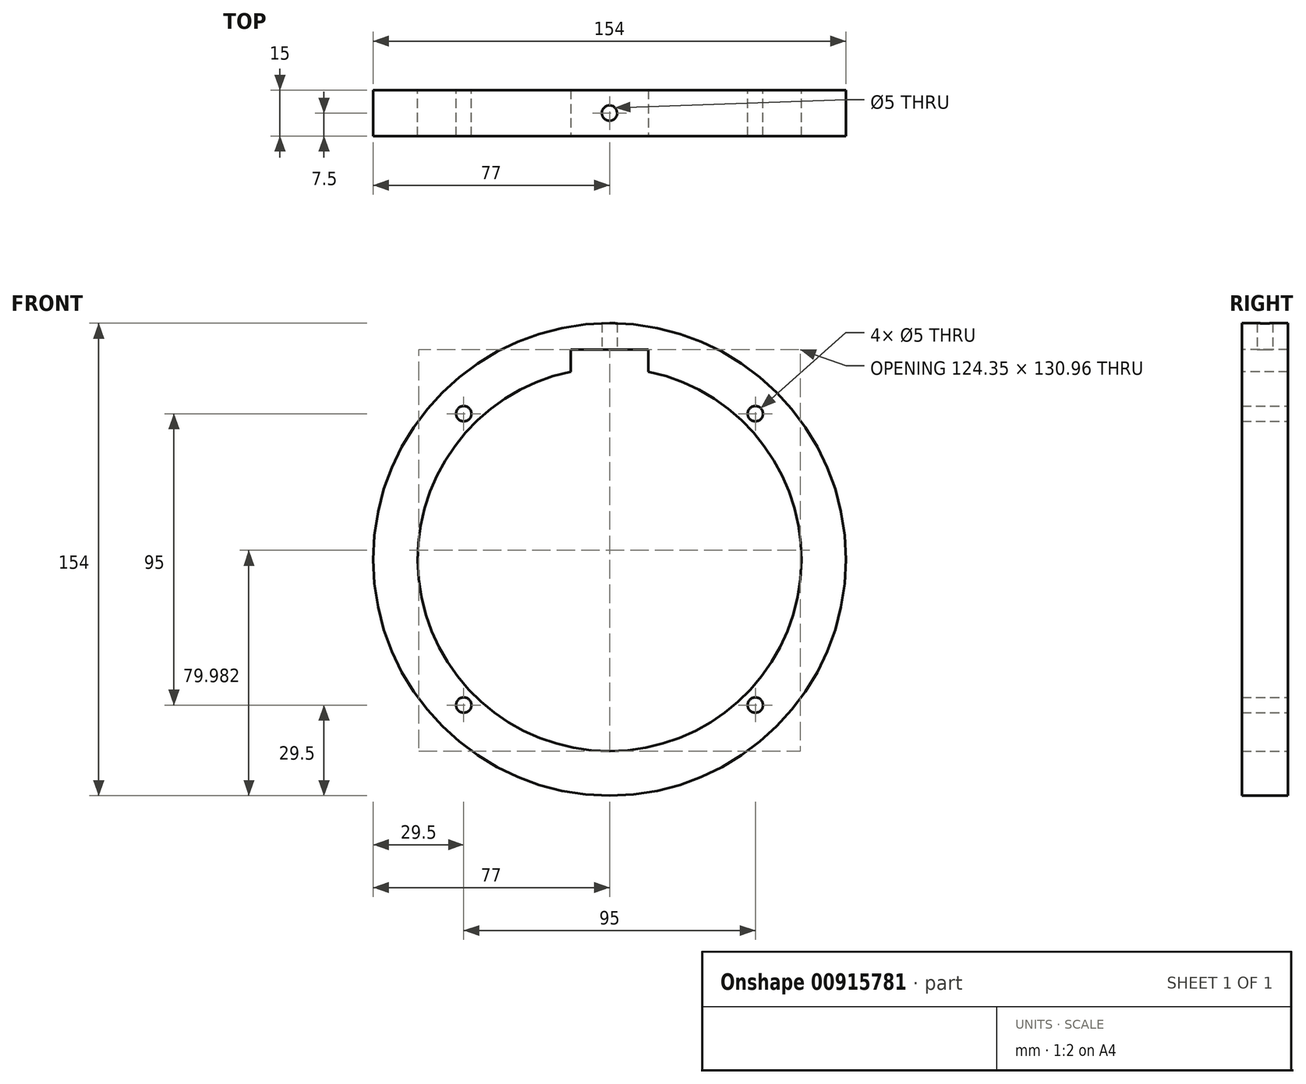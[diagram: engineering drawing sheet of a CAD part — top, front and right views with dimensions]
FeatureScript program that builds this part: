
annotation { "Feature Type Name" : "Feature", "Feature Type Description" : "" }
export const myFeature = defineFeature(function(context is Context, id is Id, definition is map)
    precondition{}
    {
        {
            var Q0;
            Q0=qCreatedBy(makeId("Front.planeOp"),FACE);
            var sketch = newSketch(context, id + "F0", { "sketchPlane" : qUnion([Q0])});
            skCircle(sketch, "E0", {"center": v(0, 0) * mm, "radius": 77 * mm});
            skCircle(sketch, "E1", {"center": v(0, 0) * mm, "radius": 62.5 * mm});
            skSolve(sketch);
        }
        {
            var Q0;
            Q0=makeQuery(id+"F0.imprint","IMPRINT",FACE,{"disambiguationData":[TD([[makeQuery(id+"F0.imprint","IMPRINT",EDGE,{"derivedFrom":sQuery(id+"F0.wireOp",EDGE,"E0")}),1.0]])]});
            extrude(context, id + "F1", {"entities" : qUnion([Q0]), "depth" : 15 * mm, "offsetDistance" : 25 * mm});
        }
        {
            var Q0;
            Q0=qCreatedBy(makeId("Front.planeOp"),FACE);
            var sketch = newSketch(context, id + "F2", { "sketchPlane" : qUnion([Q0])});
            skLineSegment(sketch, "E2.bottom", {"start": v(-47.5, 47.5) * mm, "end": v(47.5, 47.5) * mm, "construction": true});
            skLineSegment(sketch, "E2.top", {"start": v(-47.5, -47.5) * mm, "end": v(47.5, -47.5) * mm, "construction": true});
            skLineSegment(sketch, "E2.left", {"start": v(-47.5, 47.5) * mm, "end": v(-47.5, -47.5) * mm, "construction": true});
            skLineSegment(sketch, "E2.right", {"start": v(47.5, 47.5) * mm, "end": v(47.5, -47.5) * mm, "construction": true});
            skPoint(sketch, "E2.middle", {"position": v(0, 0) * mm});
            skSolve(sketch);
        }
        {
            var Q0;
            Q0=sQuery(id+"F2.wireOp",VERTEX,"E2.bottom.start");
            var Q1;
            Q1=sQuery(id+"F2.wireOp",VERTEX,"E2.bottom.end");
            var Q2;
            Q2=sQuery(id+"F2.wireOp",VERTEX,"E2.top.end");
            var Q3;
            Q3=sQuery(id+"F2.wireOp",VERTEX,"E2.top.start");
            var Q4;
            Q4=makeQuery(id+"F1.opExtrude","SWEPT_BODY",BODY,{"disambiguationData":[OSD([sQuery(id+"F0.wireOp",EDGE,"E0"),sQuery(id+"F0.wireOp",EDGE,"E1")])]});
            hole(context, id + "F3", {"style" : HoleStyle.SIMPLE, "endStyle" : HoleEndStyle.THROUGH, "oppositeDirection" : true, "holeDiameter" : 5 * mm, "majorDiameter" : 5 * mm, "isTappedThrough" : true, "tappedDepth" : 12 * mm, "tapClearance" : 3, "locations" : qUnion([Q0, Q1, Q2, Q3]), "scope" : qUnion([Q4])});
        }
        {
            var Q0;
            Q0=makeQuery(id+"F1.opExtrude","CAP_FACE",FACE,{"disambiguationData":[OSD([sQuery(id+"F0.wireOp",EDGE,"E0"),sQuery(id+"F0.wireOp",EDGE,"E1")])],"isStart":false});
            var sketch = newSketch(context, id + "F4", { "sketchPlane" : qUnion([Q0])});
            skLineSegment(sketch, "E3.bottom", {"start": v(-12.66, 68.46) * mm, "end": v(12.66, 68.46) * mm});
            skLineSegment(sketch, "E3.top", {"start": v(-12.66, 45.6) * mm, "end": v(12.66, 45.6) * mm});
            skLineSegment(sketch, "E3.left", {"start": v(-12.66, 68.46) * mm, "end": v(-12.66, 45.6) * mm});
            skLineSegment(sketch, "E3.right", {"start": v(12.66, 68.46) * mm, "end": v(12.66, 45.6) * mm});
            skPoint(sketch, "E3.middle", {"position": v(0, 57.03) * mm});
            skSolve(sketch);
        }
        {
            var Q0;
            {var subQ0=sQuery(id+"F4.wireOp",EDGE,"E3.bottom");Q0=makeQuery(id+"F4.imprint","IMPRINT",FACE,{"disambiguationData":[TD([[makeQuery(id+"F4.imprint","IMPRINT",EDGE,{"derivedFrom":subQ0}),-1.0]])]});}
            extrude(context, id + "F5", {"entities" : qUnion([Q0]), "operationType" : NewBodyOperationType.REMOVE, "oppositeDirection" : true, "depth" : 25 * mm, "offsetDistance" : 25 * mm});
        }
        {
            var Q0;
            Q0=makeQuery(id+"F5.boolean.opBoolean","COPY",FACE,{"derivedFrom":makeQuery(id+"F5.opExtrude","SWEPT_FACE",FACE,{"disambiguationData":[OSD([sQuery(id+"F4.wireOp",EDGE,"E3.bottom")])]})});
            var sketch = newSketch(context, id + "F6", { "sketchPlane" : qUnion([Q0])});
            skLineSegment(sketch, "E4", {"start": v(0, 15) * mm, "end": v(0, 0) * mm});
            skLineSegment(sketch, "E5", {"start": v(0, 0) * mm, "end": v(0, 7.5) * mm});
            skSolve(sketch);
        }
        {
            var Q0;
            Q0=sQuery(id+"F6.wireOp",VERTEX,"E5.end");
            var Q1;
            Q1=makeQuery(id+"F1.opExtrude","SWEPT_BODY",BODY,{"disambiguationData":[OSD([sQuery(id+"F0.wireOp",EDGE,"E0"),sQuery(id+"F0.wireOp",EDGE,"E1")])]});
            hole(context, id + "F7", {"style" : HoleStyle.SIMPLE, "endStyle" : HoleEndStyle.BLIND, "holeDiameter" : 5 * mm, "majorDiameter" : 5 * mm, "holeDepth" : 12 * mm, "isTappedThrough" : true, "tappedDepth" : 12 * mm, "tapClearance" : 3, "locations" : qUnion([Q0]), "scope" : qUnion([Q1])});
        }
    });
